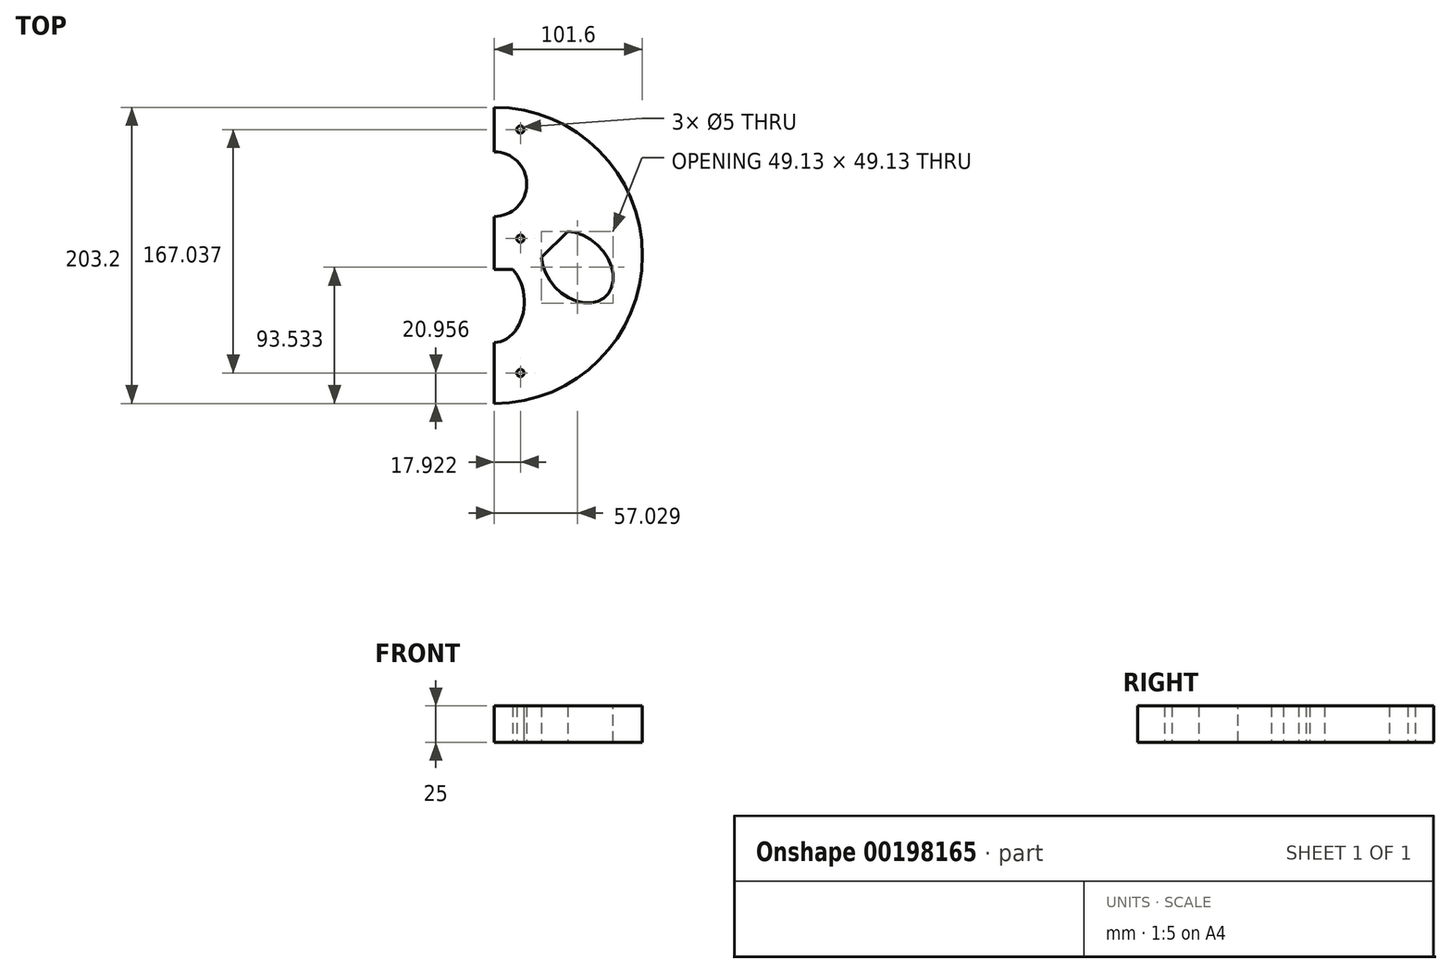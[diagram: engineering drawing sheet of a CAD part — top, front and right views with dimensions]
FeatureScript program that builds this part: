
annotation { "Feature Type Name" : "Feature", "Feature Type Description" : "" }
export const myFeature = defineFeature(function(context is Context, id is Id, definition is map)
    precondition{}
    {
        {
            var Q0;
            Q0=qCreatedBy(makeId("Top.planeOp"),FACE);
            var sketch = newSketch(context, id + "F0", { "sketchPlane" : qUnion([Q0])});
            skCircle(sketch, "E0", {"center": v(0, 0) * mm, "radius": 101.6 * mm});
            skCircle(sketch, "E1", {"center": v(0, 48.96) * mm, "radius": 22.23 * mm});
            skLineSegment(sketch, "E2", {"start": v(-12.7, -9.65) * mm, "end": v(12.7, -9.65) * mm});
            skPoint(sketch, "E3", {"position": v(0, -59.69) * mm});
            skPoint(sketch, "E4.endSnap0", {"position": v(0, -3.68) * mm});
            skLineSegment(sketch, "E5", {"start": v(0, 48.96) * mm, "end": v(-18.92, 30.04) * mm, "construction": true});
            skLineSegment(sketch, "E6", {"start": v(0, 48.96) * mm, "end": v(13.5, 35.46) * mm, "construction": true});
            skLineSegment(sketch, "E7", {"start": v(-71.57, 6.49) * mm, "end": v(-42.48, -22.61) * mm, "construction": true});
            skLineSegment(sketch, "E8", {"start": v(42.48, -22.61) * mm, "end": v(71.57, 6.49) * mm, "construction": true});
            skLineSegment(sketch, "E9", {"start": v(-20.57, -31.68) * mm, "end": v(20.57, -31.68) * mm, "construction": true});
            skLineSegment(sketch, "E10", {"start": v(-50.42, 16.5) * mm, "end": v(-32.46, -1.46) * mm});
            skLineSegment(sketch, "E11", {"start": v(32.46, -1.46) * mm, "end": v(50.42, 16.5) * mm});
            skPoint(sketch, "E12", {"position": v(-76.83, -27.86) * mm});
            skPoint(sketch, "E13", {"position": v(76.83, -27.86) * mm});
            skLineSegment(sketch, "E14", {"start": v(-41.44, 7.52) * mm, "end": v(-76.83, -27.86) * mm, "construction": true});
            skLineSegment(sketch, "E15", {"start": v(41.44, 7.52) * mm, "end": v(76.83, -27.86) * mm, "construction": true});
            skLineSegment(sketch, "E16", {"start": v(0, -9.65) * mm, "end": v(0, -59.69) * mm, "construction": true});
            skLineSegment(sketch, "E17", {"start": v(0, 71.19) * mm, "end": v(0, 101.6) * mm, "construction": true});
            skLineSegment(sketch, "E18", {"start": v(-37.22, 11.74) * mm, "end": v(-15.72, 33.25) * mm, "construction": true});
            skLineSegment(sketch, "E19", {"start": v(37.22, 11.74) * mm, "end": v(15.72, 33.25) * mm, "construction": true});
            skLineSegment(sketch, "E20", {"start": v(0, -3.68) * mm, "end": v(0, 26.74) * mm, "construction": true});
            skLineSegment(sketch, "E21", {"start": v(-34.63, -11) * mm, "end": v(-17.92, -17.93) * mm, "construction": true});
            skLineSegment(sketch, "E22", {"start": v(17.92, -17.93) * mm, "end": v(34.63, -11) * mm, "construction": true});
            skLineSegment(sketch, "E23", {"start": v(-81, -20.33) * mm, "end": v(-98.54, -24.73) * mm, "construction": true});
            skLineSegment(sketch, "E24", {"start": v(0, -101.6) * mm, "end": v(0, 101.6) * mm});
            skEllipticalArc(sketch, "E25", {});
            skEllipticalArc(sketch, "E26", {});
            skEllipticalArc(sketch, "E27", {});
            skEllipticalArc(sketch, "E28", {});
            skEllipticalArc(sketch, "E29", {});
            skEllipticalArc(sketch, "E30", {});
            skCircle(sketch, "E31", {"center": v(17.92, 86.4) * mm, "radius": 2.5 * mm});
            skCircle(sketch, "E32", {"center": v(17.92, 11.53) * mm, "radius": 2.5 * mm});
            skCircle(sketch, "E33", {"center": v(17.92, -80.64) * mm, "radius": 2.5 * mm});
            skLineSegment(sketch, "E34", {"start": v(17.92, 86.4) * mm, "end": v(0, 86.4) * mm, "construction": true});
            skLineSegment(sketch, "E35", {"start": v(17.92, 11.53) * mm, "end": v(0, 11.53) * mm, "construction": true});
            skLineSegment(sketch, "E36", {"start": v(0, -59.69) * mm, "end": v(0, -101.6) * mm, "construction": true});
            skLineSegment(sketch, "E37", {"start": v(17.92, -80.64) * mm, "end": v(0, -80.64) * mm, "construction": true});
            const initialGuessF0  = {"E25": [0.057023632784309455, -0.00806204076712544, -0.7071067811865476, 0.7071067811865475, 0.02800518687653526, 0.020574, 5.617899580550294, 0.665285726629255], "E26": [0.057023632784309455, -0.00806204076712544, -0.7071067811865476, 0.7071067811865475, 0.02800518687653526, 0.020574, 0.665285726629255, 5.617899580550294], "E27": [0, -0.03168200284217031, 0, -1, 0.028005186876535273, 0.020574, 2.476306926960537, 3.80687838021905], "E28": [0, -0.03168200284217031, 0, -1, 0.028005186876535273, 0.020574, 3.80687838021905, 2.476306926960537], "E29": [-0.057023632784309504, -0.008062040767125479, 0.7071067811865475, 0.7071067811865476, 0.028005186876535273, 0.020574, 0.6652857266292947, 5.61789958055033], "E30": [-0.057023632784309504, -0.008062040767125479, 0.7071067811865475, 0.7071067811865476, 0.028005186876535273, 0.020574, 5.61789958055033, 0.6652857266292947]};
            skSetInitialGuess(sketch, initialGuessF0);
            skSolve(sketch);
        }
        {
            var Q0;
            Q0=makeQuery(id+"F0.imprint","IMPRINT",FACE,{"disambiguationData":[TD([[makeQuery(id+"F0.imprint","IMPRINT",EDGE,{"derivedFrom":sQuery(id+"F0.wireOp",EDGE,"E25")}),-1.0]])]});
            var Q1;
            {var subQ1=sQuery(id+"F0.wireOp",EDGE,"E2");var subQ3=sQuery(id+"F0.wireOp",EDGE,"E24");var subQ4=makeQuery(id+"F0.imprint","INTERSECT",VERTEX,{"derivedFrom":[subQ1,subQ3]});Q1=makeQuery(id+"F0.imprint","IMPRINT",FACE,{"disambiguationData":[TD([[makeQuery(id+"F0.imprint","IMPRINT",EDGE,{"disambiguationData":[TD([[subQ4,-1.0]])],"derivedFrom":subQ3}),-1.0]])]});}
            var Q2;
            Q2=makeQuery(id+"F0.imprint","IMPRINT",FACE,{"disambiguationData":[TD([[makeQuery(id+"F0.imprint","IMPRINT",EDGE,{"derivedFrom":sQuery(id+"F0.wireOp",EDGE,"E11")}),1.0]])]});
            extrude(context, id + "F1", {"entities" : qUnion([Q0, Q1, Q2]), "depth" : 25 * mm});
        }
    });
